# Revit family: LEPC14
name_source: partatom
category: Lighting Fixtures
units: mm (PartAtom-declared; Revit-internal decimal feet)

## family parameters
Cut with Voids When Loaded = No
Host = Face
Light Source = Yes
OmniClass Number = 23.80.70.11
OmniClass Title = Luminaries for Internal Lighting
Part Type = Normal
Room Calculation Point = No
Round Connector Dimension = Use Diameter
Shared = Yes

## types (1)
- LEPC14-40VL-LL
    Apparent Load = 0 VA
    Backbox = White
    Color Filter = 16777215
    Default Elevation = 4.00'
    Description = A e•poc® LED full distribution luminaire, with advanced solid state electronics, has significantly improved performance to offer additional lumen packages for maximum versatility.
    Dimming Lamp Color Temperature Shift = <None>
    Emit from Line Length = 2.00'
    Glass = White Glass
    Lamp = LED LAMP
    Lumens Output = Very High Lumen
    Manufacturer = Columbia Lighting
    Model = LEPC14
    Nominal Watts = 62 W
    Photometric Web File = LEPC14-40VL-LL.ies
    Row Length = 4.00'
    Shielding = Low Lamp Image
    Tilt Angle = -90.00°
    URL = https://www.currentlighting.com
    Voltage = 120 V

## geometry (parser evidence)
native form markers: Sweep x3
no freeform markers — native parametric forms only
